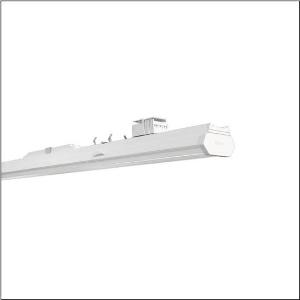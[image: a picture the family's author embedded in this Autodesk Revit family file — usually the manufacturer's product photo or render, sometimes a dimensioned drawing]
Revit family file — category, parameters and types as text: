
# Revit family: licross_r__11_protected_mo_51td12cn49xg_1fdf
name_source: partatom
category: Lighting Fixtures
units: mm (PartAtom-declared; Revit-internal decimal feet)

## family parameters
Cut with Voids When Loaded = No
Host = Face
Light Source = No
Part Type = Normal
Room Calculation Point = No
Round Connector Dimension = Use Diameter
Shared = No

## types (1)
- --- (1 x LED, 9070 lm, 49.4 W, 4000K)
    Apparent Load = 49 VA
    CIE Flux Codes = 73 92 98 99 100
    Color Rendering = 80
    Color Temperature = 4000K
    Default Elevation = 1800 mm
    Description = Licross® 11 Protected MO, luminaire insert, of sheet steel, galvanised, coil coated, white, length: 1.500mm, width: 90mm, height: 101mm, LED rated luminous flux: 9.070lm, light colour: 840, control gear: ON/OFF Multilumen, CLOi, with plug, 3-pole, with phase selection, mains connection: 220..240V, AC, 50/60Hz, start of lifetime: 49W, end of service life: 55W, halogen-free wiring, primary light control with lens, of plastic, primary optical cover: cover, of PMMA, light emission: direct distribution, primary light characteristic: symmetric, protection rating (complete): IP54, insulation class (complete): insulation class I (protective earthing), certification: CE, ENEC, VDE, UKCA, protection symbol: D if used in an environment with non-conductive dust loads with corresponding accessories, impact resistance: IK06, permissible ambient temperature for indoor applications: -35..+40°C, corresponds to IFS (International Featured Standards) requirements for safety and quality in the food industry, reducing of maximum allowable ambient temperature of 5°C with ceiling mounting, LABS conformity tested according to VDMA 24364:2018-05, packaging unit: 1 piece
    Height = 92 mm
    Lamp = 1 x LED
    Lamp Light Flux = 9070 lm
    Lamp Power = 49.4 W
    Lamp count = 1
    Length = 1500 mm
    Luminous efficacy = 184 lm/W
    Manufacturer = Siteco
    ModVariant = No
    Model = 51TD12CN49XG
    Mounting Place = Ceiling
    Mounting Type = Pendant
    Number of Poles = 1
    OnlyDefault = Yes
    Power Factor = 1
    Product Name = Licross® 11 Protected MO
    Product group = luminaire insert
    ProductGroupID = 901
    Protection Class = Protection class I
    Protection Degree = IP 54
    RLX_Detail_Level = 1
    RLX_Emergency_Light_Flux = 0 lm
    RLX_Emergency_Type = 0
    RLX_Emergency_Type_DB = No
    RlxData = <blob elided: 22061 chars, md5=787e13a5>
    Socket = socket
    Standby Power = 0 W
    System Light Flux = 9070 lm
    System Power = 49 W
    Type Comments = factory setting: luminous flux: 100 % | (A | C | E) | 113 mA
    Type Image = l_1256145.jpg
    URL = http://relux.com
    VarID = @adj_019411
    Voltage = 0 V
    Weight = 0.00 kg
    Width = 88 mm

## geometry (parser evidence)
native form markers: Blend x4, Sweep x10
no freeform markers — native parametric forms only
